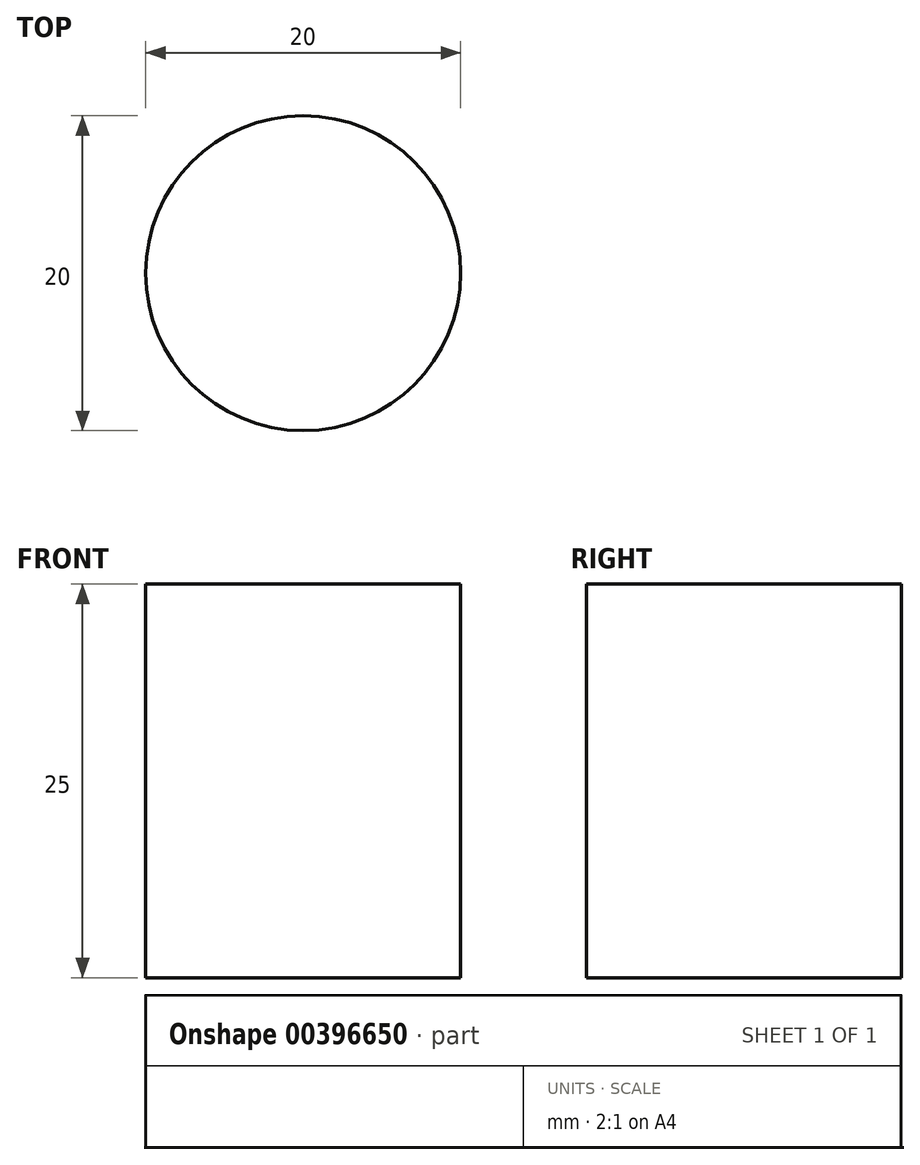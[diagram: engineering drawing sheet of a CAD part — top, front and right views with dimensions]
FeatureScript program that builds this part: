
annotation { "Feature Type Name" : "Feature", "Feature Type Description" : "" }
export const myFeature = defineFeature(function(context is Context, id is Id, definition is map)
    precondition{}
    {
        {
            var Q0;
            Q0=qCreatedBy(makeId("Top.planeOp"),FACE);
            var sketch = newSketch(context, id + "F0", { "sketchPlane" : qUnion([Q0])});
            skCircle(sketch, "E0", {"center": v(0, 0) * mm, "radius": 10 * mm});
            skSolve(sketch);
        }
        {
            var Q0;
            Q0=makeQuery(id+"F0.imprint","IMPRINT",FACE,{"disambiguationData":[TD([[makeQuery(id+"F0.imprint","IMPRINT",EDGE,{"derivedFrom":sQuery(id+"F0.wireOp",EDGE,"E0")}),1.0]])]});
            extrude(context, id + "F1", {"entities" : qUnion([Q0]), "oppositeDirection" : true, "depth" : 25 * mm});
        }
    });
